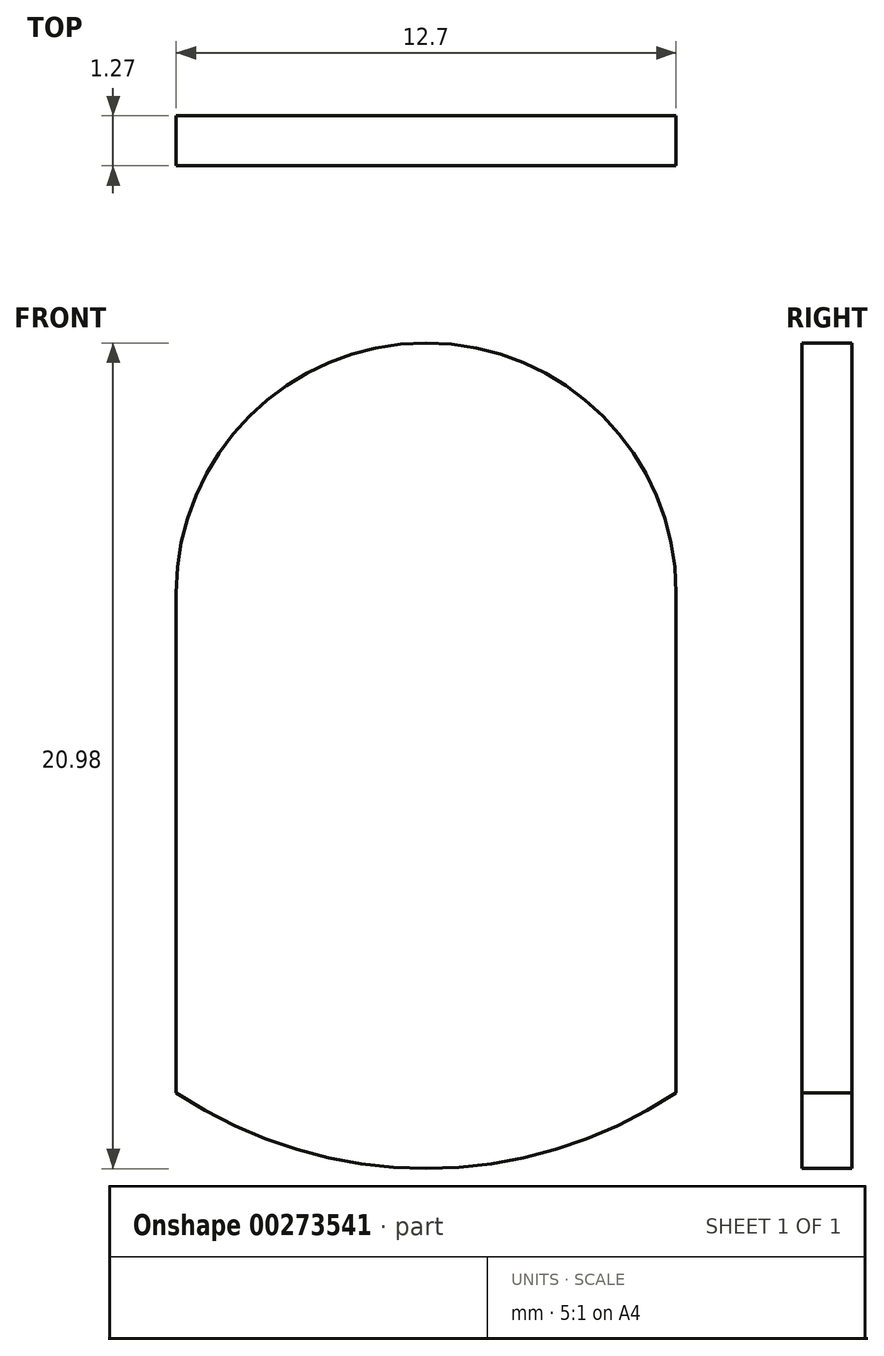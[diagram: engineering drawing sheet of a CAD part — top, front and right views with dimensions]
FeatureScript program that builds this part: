
annotation { "Feature Type Name" : "Feature", "Feature Type Description" : "" }
export const myFeature = defineFeature(function(context is Context, id is Id, definition is map)
    precondition{}
    {
        {
            var Q0;
            Q0=qCreatedBy(makeId("Front.planeOp"),FACE);
            var sketch = newSketch(context, id + "F0", { "sketchPlane" : qUnion([Q0])});
            skLineSegment(sketch, "E0", {"start": v(-12.7, 0) * mm, "end": v(-12.7, -12.7) * mm});
            skLineSegment(sketch, "E1", {"start": v(0, 0) * mm, "end": v(0, -12.7) * mm});
            skArc(sketch, "E2", {"start": v(0, 0) * mm, "mid": v(-6.35, 6.35) * mm, "end": v(-12.7, 0) * mm});
            skArc(sketch, "E3", {"start": v(-12.7, -12.7) * mm, "mid": v(-6.35, -14.63) * mm, "end": v(0, -12.7) * mm});
            skSolve(sketch);
        }
        {
            var Q0;
            Q0=makeQuery(id+"F0.imprint","IMPRINT",FACE,{"disambiguationData":[TD([[makeQuery(id+"F0.imprint","IMPRINT",EDGE,{"derivedFrom":sQuery(id+"F0.wireOp",EDGE,"E0")}),1.0]])]});
            extrude(context, id + "F1", {"entities" : qUnion([Q0]), "depth" : 1.27 * mm});
        }
    });
